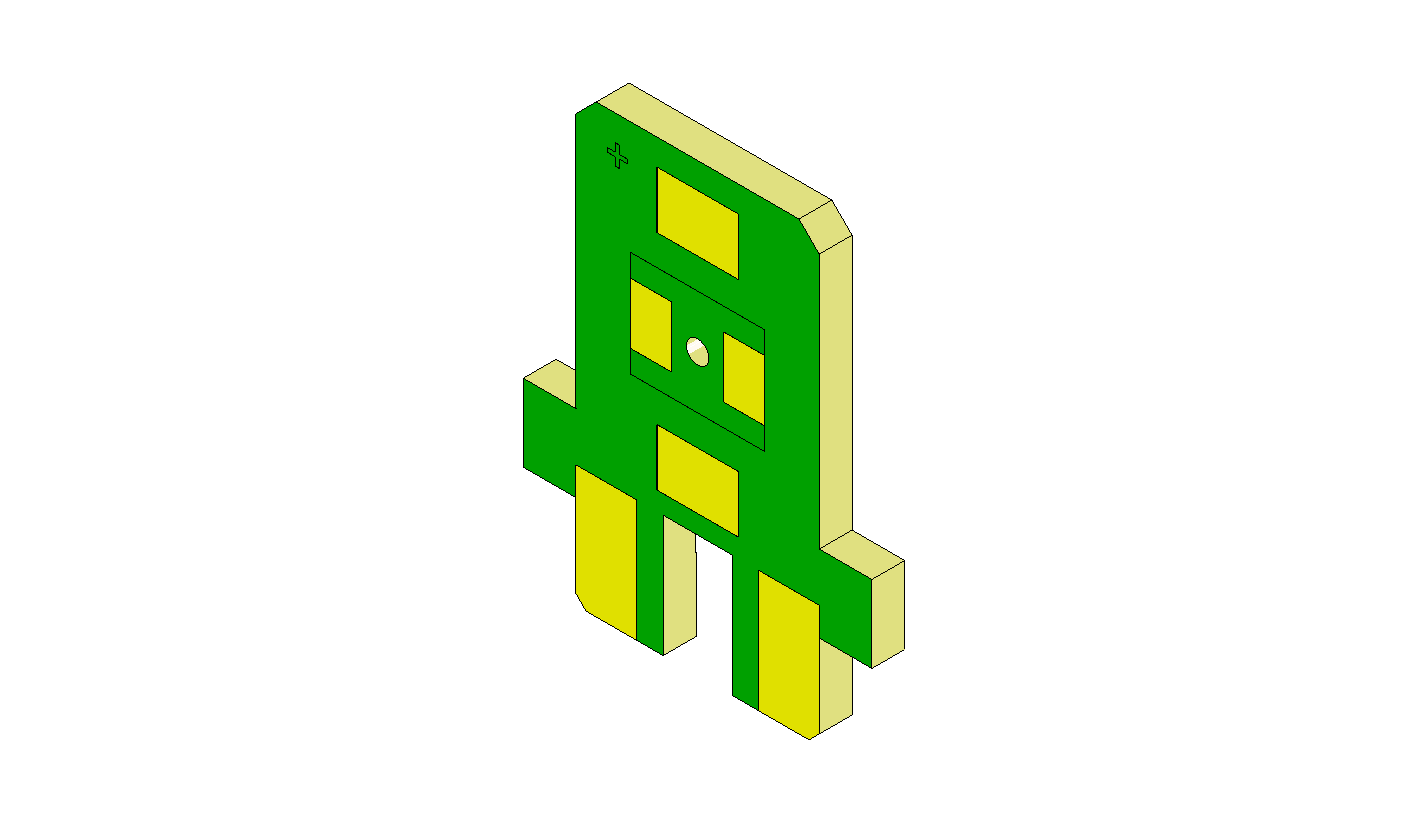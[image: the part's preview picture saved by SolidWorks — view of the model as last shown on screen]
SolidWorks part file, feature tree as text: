
SOLIDWORKS PART (.sldprt)
format: sldprt  version: not decoded by parser v0  size: 739,840 bytes
history: native  units: mm
features: sketch x5, extrude x3, chamfer x2, cut_extrude x2, material x1 (+11 scaffold rows collapsed)
feature tree (24):
  scaffold x11  (default folders/planes/origin — collapsed)
  material  "Material <not specified>"
  sketch  "Sketch1"  dims[D1=3.0mm D2=6.0mm D3=8.0mm D4=1.7mm D5=1.9mm D6=8.6mm D7=8.7mm D8=1.3mm]
  extrude  "Extrude1"  Depth=0.81mm
  chamfer  "Chamfer1"  Distance=0.5mm Angle=45deg
  sketch  "Sketch2"  dims[D1=1.5mm D2=2.0mm D3=1.4mm D4=1.5mm D5=3.3mm D6=4.16mm D7=5.5mm D8=1.0mm]
  extrude  "Extrude2"  Depth=0.001mm
  chamfer  "Chamfer2"  Distance=0.25mm Angle=45deg
  sketch  "Sketch3"  dims[D1=1.3mm D2=6.91mm D3=0.1mm D4=0.5mm D5=~0.603714mm]
  cut_extrude  "Cut-Extrude1"  Depth=0.001mm
  sketch  "Sketch4"  dims[D1=1.8mm]
  extrude  "Extrude3"  Depth=0.001mm
  sketch  "Sketch5"  dims[D1=0.5588mm]
  cut_extrude  "Cut-Extrude2"  [1 undecoded]
decode coverage: 11 of 12 modeling features carry decoded parameters
note: ~ marks probable driven/reference dimensions
note: 1 parameter value undecoded
note: suppression state not decoded; provenance and decode notes live in map.json
